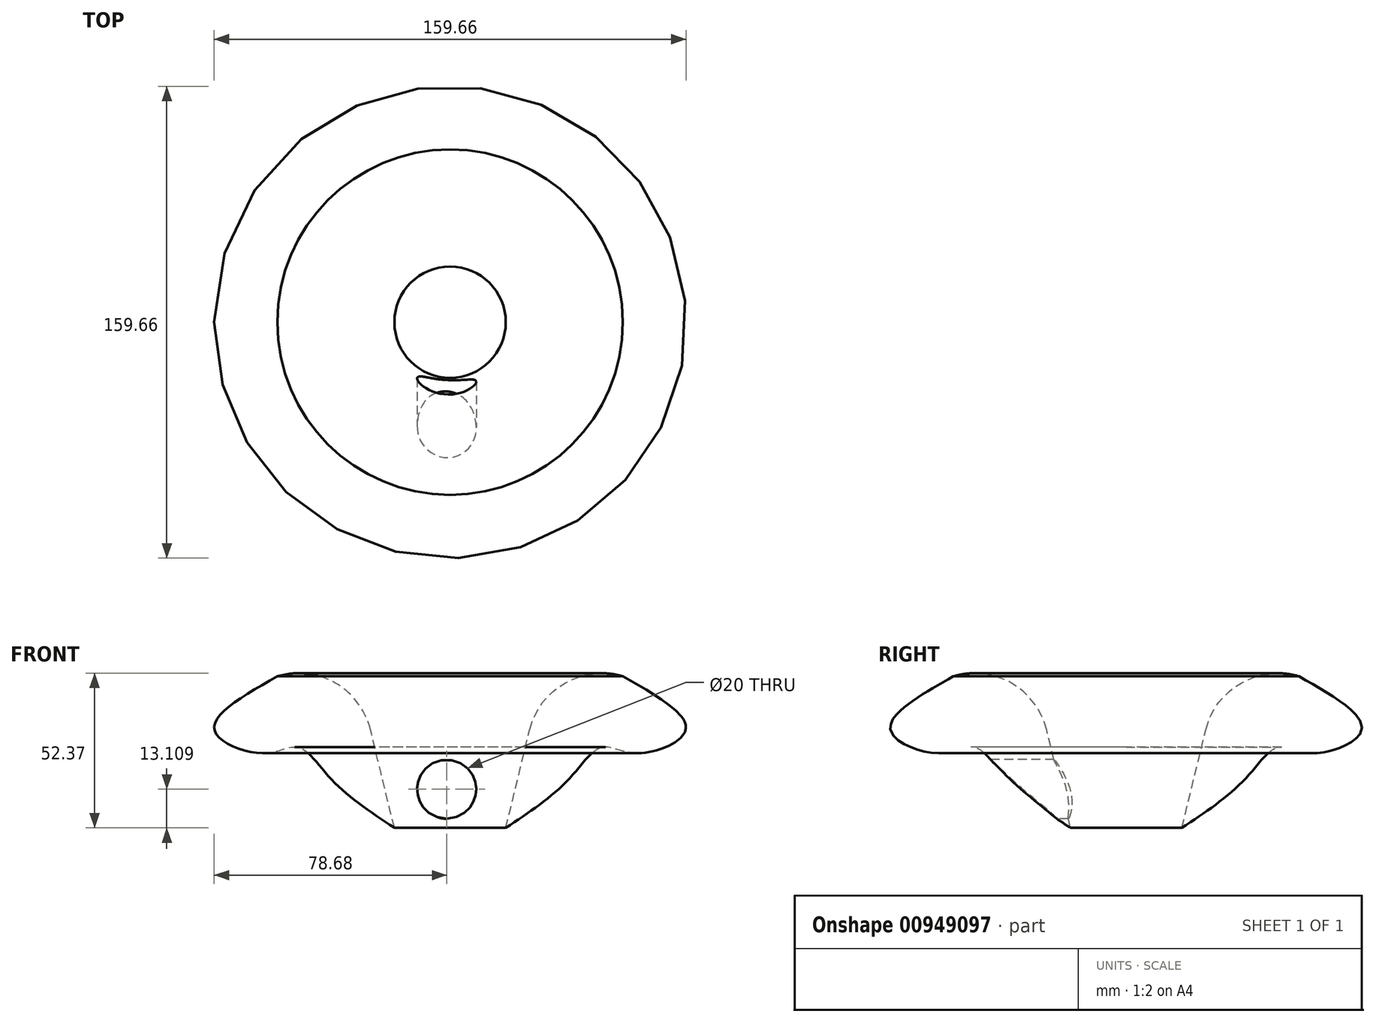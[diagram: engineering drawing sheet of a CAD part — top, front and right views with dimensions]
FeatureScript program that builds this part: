
annotation { "Feature Type Name" : "Feature", "Feature Type Description" : "" }
export const myFeature = defineFeature(function(context is Context, id is Id, definition is map)
    precondition{}
    {
        {
            var Q0;
            Q0=qCreatedBy(makeId("Front.planeOp"),FACE);
            var sketch = newSketch(context, id + "F0", { "sketchPlane" : qUnion([Q0])});
            skLineSegment(sketch, "E0", {"start": v(0, 0) * mm, "end": v(8.08, 33.2) * mm});
            skArc(sketch, "E1", {"start": v(39.6, 51.33) * mm, "mid": v(19.96, 49.03) * mm, "end": v(8.08, 33.2) * mm});
            skFitSpline(sketch, "E2", {"points": [v(39.6, 51.33) * mm, v(60.9, 33.2) * mm, v(44.34, 25.32) * mm, v(32.47, 27.26) * mm, v(21.48, 16.65) * mm, v(0, 0) * mm], "startDerivative": vector(141.3, -80.26) * mm, "endDerivative": vector(-100.28, -66.87) * mm});
            skLineSegment(sketch, "E3", {"start": v(-18.85, 25.88) * mm, "end": v(-18.85, 54.77) * mm});
            skSolve(sketch);
        }
        {
            var Q0;
            Q0=makeQuery(id+"F0.imprint","IMPRINT",FACE,{"disambiguationData":[TD([[makeQuery(id+"F0.imprint","IMPRINT",EDGE,{"derivedFrom":sQuery(id+"F0.wireOp",EDGE,"E0")}),-1.0]])]});
            var Q1;
            Q1=sQuery(id+"F0.wireOp",EDGE,"E3");
            revolve(context, id + "F1", {"surfaceOperationType" : NewSurfaceOperationType.NEW, "entities" : qUnion([Q0]), "axis" : qUnion([Q1]), "revolveType" : RevolveType.FULL});
        }
        {
            var Q0;
            Q0=qCreatedBy(makeId("Front.planeOp"),FACE);
            cPlane(context, id + "F2", {"entities" : qUnion([Q0]), "cplaneType" : CPlaneType.OFFSET, "offset" : 80 * mm, "width" : 150 * mm, "height" : 150 * mm});
        }
        {
            var Q0;
            Q0=qCreatedBy(id+"F2.planeOp",FACE);
            var sketch = newSketch(context, id + "F3", { "sketchPlane" : qUnion([Q0])});
            skCircle(sketch, "E4", {"center": v(-20, 13.1) * mm, "radius": 10 * mm});
            skSolve(sketch);
        }
        {
            var Q0;
            Q0=makeQuery(id+"F3.imprint","IMPRINT",FACE,{"disambiguationData":[TD([[makeQuery(id+"F3.imprint","IMPRINT",EDGE,{"derivedFrom":sQuery(id+"F3.wireOp",EDGE,"E4")}),1.0]])]});
            extrude(context, id + "F4", {"entities" : qUnion([Q0]), "operationType" : NewBodyOperationType.REMOVE, "oppositeDirection" : true, "depth" : 70 * mm, "offsetDistance" : 25 * mm});
        }
    });
